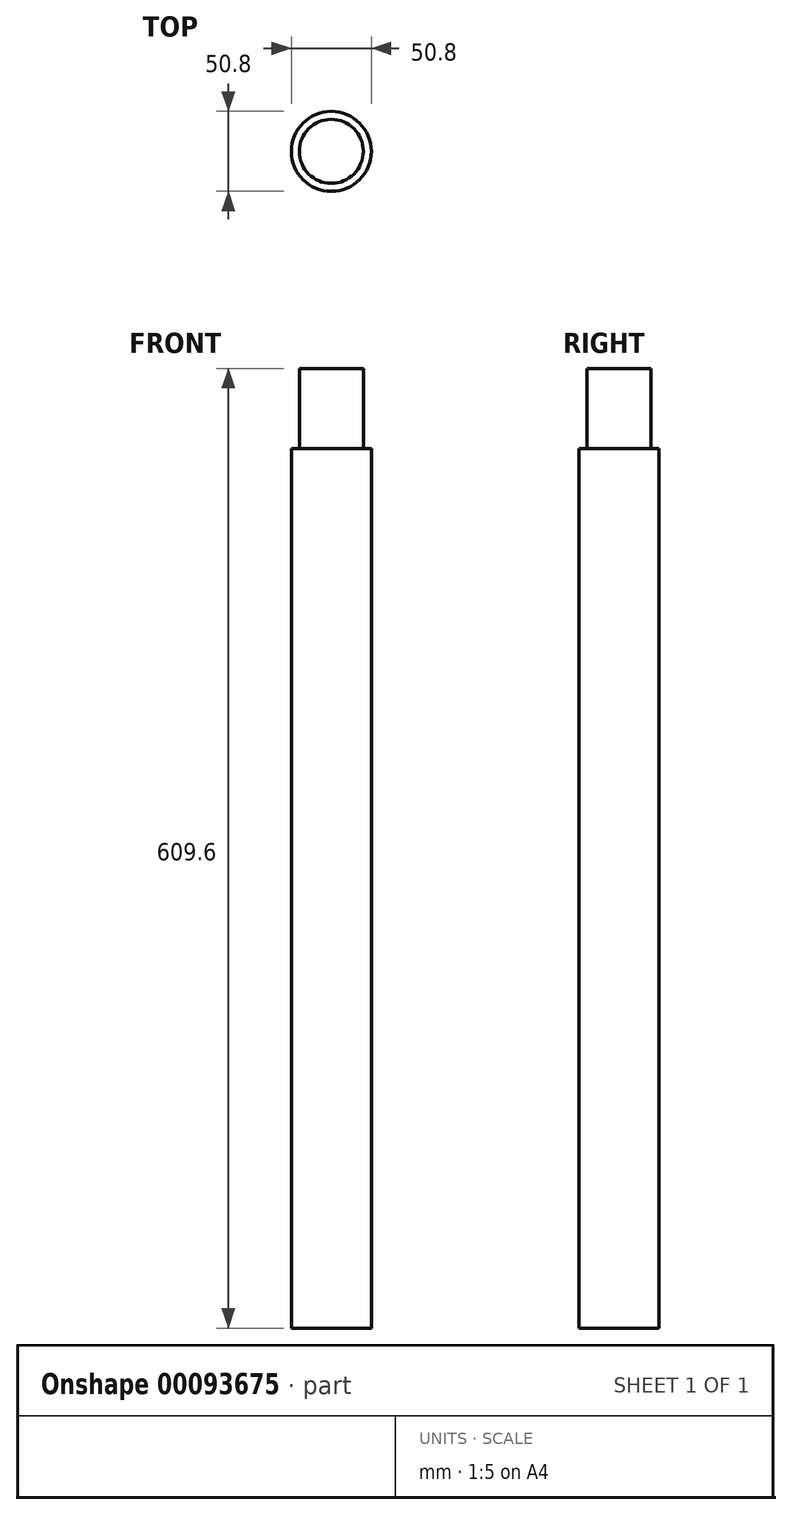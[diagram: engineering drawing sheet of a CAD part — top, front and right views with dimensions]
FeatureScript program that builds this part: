
annotation { "Feature Type Name" : "Feature", "Feature Type Description" : "" }
export const myFeature = defineFeature(function(context is Context, id is Id, definition is map)
    precondition{}
    {
        {
            var Q0;
            Q0=qCreatedBy(makeId("Top.planeOp"),FACE);
            var sketch = newSketch(context, id + "F0", { "sketchPlane" : qUnion([Q0])});
            skCircle(sketch, "E0", {"center": v(0, 0) * mm, "radius": 25.4 * mm});
            skCircle(sketch, "E1", {"center": v(0, 0) * mm, "radius": 19.05 * mm, "construction": true});
            skSolve(sketch);
        }
        {
            var Q0;
            Q0=makeQuery(id+"F0.imprint","IMPRINT",FACE,{"disambiguationData":[TD([[makeQuery(id+"F0.imprint","IMPRINT",EDGE,{"derivedFrom":sQuery(id+"F0.wireOp",EDGE,"E0")}),1.0]])]});
            extrude(context, id + "F1", {"entities" : qUnion([Q0]), "depth" : 609.6 * mm});
        }
        {
            var Q0;
            Q0=makeQuery(id+"F1.opExtrude","CAP_FACE",FACE,{"disambiguationData":[OSD([sQuery(id+"F0.wireOp",EDGE,"E0")])],"isStart":false});
            var sketch = newSketch(context, id + "F2", { "sketchPlane" : qUnion([Q0])});
            skCircle(sketch, "E2", {"center": v(0, 0) * mm, "radius": 20.32 * mm});
            skCircle(sketch, "E3.0", {"center": v(0, 0) * mm, "radius": 25.4 * mm});
            skSolve(sketch);
        }
        {
            var Q0;
            Q0=qSketchRegion(id+"F2",true);
            extrude(context, id + "F3", {"entities" : qUnion([Q0]), "operationType" : NewBodyOperationType.REMOVE, "oppositeDirection" : true, "depth" : 50.8 * mm});
        }
    });
